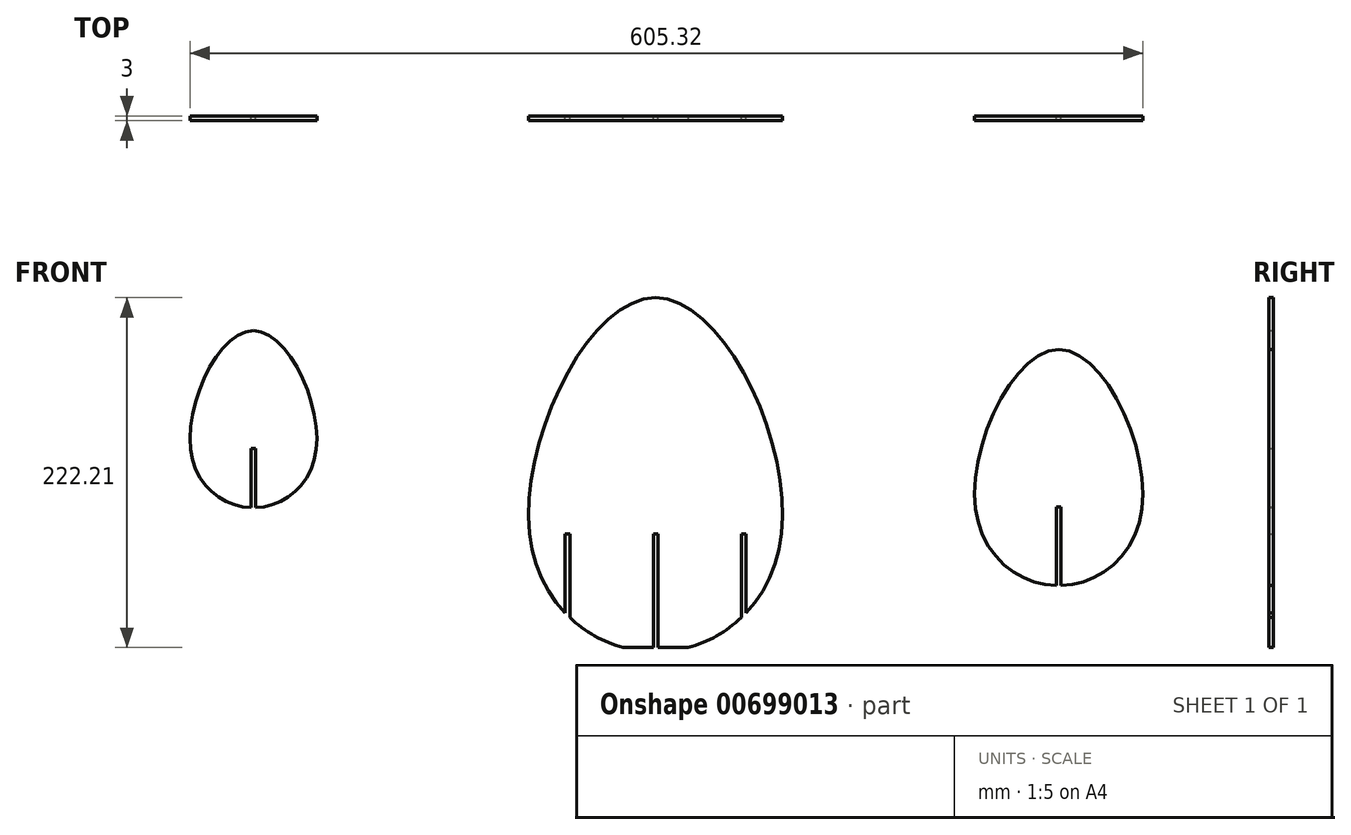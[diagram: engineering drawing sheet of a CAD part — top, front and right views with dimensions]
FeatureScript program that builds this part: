
annotation { "Feature Type Name" : "Feature", "Feature Type Description" : "" }
export const myFeature = defineFeature(function(context is Context, id is Id, definition is map)
    precondition{}
    {
        {
            var Q0;
            Q0=qCreatedBy(makeId("Front.planeOp"),FACE);
            var sketch = newSketch(context, id + "F0", { "sketchPlane" : qUnion([Q0])});
            skLineSegment(sketch, "E0", {"start": v(0, 0) * mm, "end": v(-80, 0) * mm, "construction": true});
            skLineSegment(sketch, "E1", {"start": v(0, 0) * mm, "end": v(0, -75) * mm});
            skLineSegment(sketch, "E2", {"start": v(0, 0) * mm, "end": v(80, 0) * mm, "construction": true});
            skLineSegment(sketch, "E3", {"start": v(0, 0) * mm, "end": v(0, 150) * mm});
            skFitSpline(sketch, "E4", {"points": [v(0, 150) * mm, v(-80, 0) * mm, v(0, -75) * mm, v(80, 0) * mm, v(0, 150) * mm]});
            skLineSegment(sketch, "E5", {"start": v(-20.64, -72.2) * mm, "end": v(20.64, -72.2) * mm});
            skLineSegment(sketch, "E6", {"start": v(-255.53, 54.14) * mm, "end": v(-295.53, 54.14) * mm, "construction": true});
            skLineSegment(sketch, "E7", {"start": v(-255.53, 54.14) * mm, "end": v(-255.53, 16.64) * mm});
            skLineSegment(sketch, "E8", {"start": v(-255.53, 54.14) * mm, "end": v(-215.53, 54.14) * mm, "construction": true});
            skLineSegment(sketch, "E9", {"start": v(-255.53, 54.14) * mm, "end": v(-255.53, 129.14) * mm});
            skFitSpline(sketch, "E10", {"points": [v(-255.53, 129.14) * mm, v(-295.53, 54.14) * mm, v(-255.53, 16.64) * mm, v(-215.53, 54.14) * mm, v(-255.53, 129.14) * mm]});
            skLineSegment(sketch, "E11", {"start": v(256.02, 17.1) * mm, "end": v(203.02, 17.1) * mm, "construction": true});
            skLineSegment(sketch, "E12", {"start": v(256.02, 17.1) * mm, "end": v(256.02, -32.9) * mm});
            skLineSegment(sketch, "E13", {"start": v(256.02, 17.1) * mm, "end": v(309.02, 17.1) * mm, "construction": true});
            skLineSegment(sketch, "E14", {"start": v(256.02, 17.1) * mm, "end": v(256.02, 117.1) * mm});
            skFitSpline(sketch, "E15", {"points": [v(256.02, 117.1) * mm, v(203.02, 17.1) * mm, v(256.02, -32.9) * mm, v(309.02, 17.1) * mm, v(256.02, 117.1) * mm]});
            skLineSegment(sketch, "E16.bottom", {"start": v(254.52, 17.1) * mm, "end": v(257.52, 17.1) * mm});
            skLineSegment(sketch, "E16.top", {"start": v(254.52, -35.3) * mm, "end": v(257.52, -35.3) * mm});
            skLineSegment(sketch, "E16.left", {"start": v(254.52, 17.1) * mm, "end": v(254.52, -35.3) * mm});
            skLineSegment(sketch, "E16.right", {"start": v(257.52, 17.1) * mm, "end": v(257.52, -35.3) * mm});
            skLineSegment(sketch, "E17.bottom", {"start": v(-257.03, 54.14) * mm, "end": v(-254.03, 54.14) * mm});
            skLineSegment(sketch, "E17.top", {"start": v(-257.03, 14.08) * mm, "end": v(-254.03, 14.08) * mm});
            skLineSegment(sketch, "E17.left", {"start": v(-257.03, 54.14) * mm, "end": v(-257.03, 14.08) * mm});
            skLineSegment(sketch, "E17.right", {"start": v(-254.03, 54.14) * mm, "end": v(-254.03, 14.08) * mm});
            skLineSegment(sketch, "E18", {"start": v(54.5, -277) * mm, "end": v(-25.5, -277) * mm, "construction": true});
            skLineSegment(sketch, "E19", {"start": v(54.5, -277) * mm, "end": v(54.5, -352) * mm});
            skLineSegment(sketch, "E20", {"start": v(54.5, -277) * mm, "end": v(134.5, -277) * mm, "construction": true});
            skLineSegment(sketch, "E21", {"start": v(54.5, -277) * mm, "end": v(54.5, -127) * mm});
            skFitSpline(sketch, "E22", {"points": [v(54.5, -127) * mm, v(-25.5, -277) * mm, v(54.5, -352) * mm, v(134.5, -277) * mm, v(54.5, -127) * mm]});
            skLineSegment(sketch, "E23", {"start": v(33.86, -349.21) * mm, "end": v(75.14, -349.21) * mm});
            skLineSegment(sketch, "E24", {"start": v(-211.8, -225.01) * mm, "end": v(-251.8, -225.01) * mm, "construction": true});
            skLineSegment(sketch, "E25", {"start": v(-211.8, -225.01) * mm, "end": v(-211.8, -262.51) * mm});
            skLineSegment(sketch, "E26", {"start": v(-211.8, -225.01) * mm, "end": v(-171.8, -225.01) * mm, "construction": true});
            skLineSegment(sketch, "E27", {"start": v(-211.8, -225.01) * mm, "end": v(-211.8, -150.01) * mm});
            skFitSpline(sketch, "E28", {"points": [v(-211.8, -150.01) * mm, v(-251.8, -225.01) * mm, v(-211.8, -262.51) * mm, v(-171.8, -225.01) * mm, v(-211.8, -150.01) * mm]});
            skLineSegment(sketch, "E29", {"start": v(299.74, -262.05) * mm, "end": v(246.74, -262.05) * mm, "construction": true});
            skLineSegment(sketch, "E30", {"start": v(299.74, -262.05) * mm, "end": v(299.74, -312.05) * mm});
            skLineSegment(sketch, "E31", {"start": v(299.74, -262.05) * mm, "end": v(352.74, -262.05) * mm, "construction": true});
            skLineSegment(sketch, "E32", {"start": v(299.74, -262.05) * mm, "end": v(299.74, -162.05) * mm});
            skFitSpline(sketch, "E33", {"points": [v(299.74, -162.05) * mm, v(246.74, -262.05) * mm, v(299.74, -312.05) * mm, v(352.74, -262.05) * mm, v(299.74, -162.05) * mm]});
            skLineSegment(sketch, "E34.bottom", {"start": v(298.24, -262.05) * mm, "end": v(301.24, -262.05) * mm});
            skLineSegment(sketch, "E35.bottom", {"start": v(-213.3, -225.01) * mm, "end": v(-210.3, -225.01) * mm});
            skLineSegment(sketch, "E36.bottom", {"start": v(-1.5, 0) * mm, "end": v(1.5, 0) * mm});
            skLineSegment(sketch, "E36.top", {"start": v(-1.5, -77.56) * mm, "end": v(1.5, -77.56) * mm});
            skLineSegment(sketch, "E36.left", {"start": v(-1.5, 0) * mm, "end": v(-1.5, -77.56) * mm});
            skLineSegment(sketch, "E36.right", {"start": v(1.5, 0) * mm, "end": v(1.5, -77.56) * mm});
            skLineSegment(sketch, "E37.bottom", {"start": v(56, -277) * mm, "end": v(53, -277) * mm});
            skLineSegment(sketch, "E37.top", {"start": v(56, -127.78) * mm, "end": v(53, -127.78) * mm});
            skLineSegment(sketch, "E37.left", {"start": v(56, -277) * mm, "end": v(56, -127.78) * mm});
            skLineSegment(sketch, "E37.right", {"start": v(53, -277) * mm, "end": v(53, -127.78) * mm});
            skLineSegment(sketch, "E38.bottom", {"start": v(301.24, -262.05) * mm, "end": v(298.24, -262.05) * mm});
            skLineSegment(sketch, "E38.top", {"start": v(301.24, -159.13) * mm, "end": v(298.24, -159.13) * mm});
            skLineSegment(sketch, "E38.left", {"start": v(301.24, -262.05) * mm, "end": v(301.24, -159.13) * mm});
            skLineSegment(sketch, "E38.right", {"start": v(298.24, -262.05) * mm, "end": v(298.24, -159.13) * mm});
            skLineSegment(sketch, "E39.top", {"start": v(-213.3, -147.5) * mm, "end": v(-210.3, -147.5) * mm});
            skLineSegment(sketch, "E39.left", {"start": v(-213.3, -225.01) * mm, "end": v(-213.3, -147.5) * mm});
            skLineSegment(sketch, "E39.right", {"start": v(-210.3, -225.01) * mm, "end": v(-210.3, -147.5) * mm});
            skLineSegment(sketch, "E40.bottom", {"start": v(0, -277) * mm, "end": v(-3, -277) * mm});
            skLineSegment(sketch, "E40.top", {"start": v(0, -167) * mm, "end": v(-3, -167) * mm});
            skLineSegment(sketch, "E40.left", {"start": v(0, -277) * mm, "end": v(0, -167) * mm});
            skLineSegment(sketch, "E40.right", {"start": v(-3, -277) * mm, "end": v(-3, -167) * mm});
            skLineSegment(sketch, "E41.bottom", {"start": v(109, -277) * mm, "end": v(112, -277) * mm});
            skLineSegment(sketch, "E41.top", {"start": v(109, -167) * mm, "end": v(112, -167) * mm});
            skLineSegment(sketch, "E41.left", {"start": v(109, -277) * mm, "end": v(109, -167) * mm});
            skLineSegment(sketch, "E41.right", {"start": v(112, -277) * mm, "end": v(112, -167) * mm});
            skLineSegment(sketch, "E42.bottom", {"start": v(-54.5, 0) * mm, "end": v(-57.5, 0) * mm});
            skLineSegment(sketch, "E42.top", {"start": v(-54.5, -55) * mm, "end": v(-57.5, -55) * mm});
            skLineSegment(sketch, "E42.left", {"start": v(-54.5, 0) * mm, "end": v(-54.5, -55) * mm});
            skLineSegment(sketch, "E42.right", {"start": v(-57.5, 0) * mm, "end": v(-57.5, -55) * mm});
            skLineSegment(sketch, "E43.bottom", {"start": v(54.5, 0) * mm, "end": v(57.5, 0) * mm});
            skLineSegment(sketch, "E43.top", {"start": v(54.5, -55) * mm, "end": v(57.5, -55) * mm});
            skLineSegment(sketch, "E43.left", {"start": v(54.5, 0) * mm, "end": v(54.5, -55) * mm});
            skLineSegment(sketch, "E43.right", {"start": v(57.5, 0) * mm, "end": v(57.5, -55) * mm});
            skSolve(sketch);
        }
        {
            var Q0;
            {var subQ0=sQuery(id+"F0.wireOp",EDGE,"E3");Q0=makeQuery(id+"F0.imprint","IMPRINT",FACE,{"disambiguationData":[TD([[makeQuery(id+"F0.imprint","IMPRINT",EDGE,{"derivedFrom":subQ0}),1.0]])]});}
            var Q1;
            {var subQ0=sQuery(id+"F0.wireOp",EDGE,"E3");Q1=makeQuery(id+"F0.imprint","IMPRINT",FACE,{"disambiguationData":[TD([[makeQuery(id+"F0.imprint","IMPRINT",EDGE,{"derivedFrom":subQ0}),-1.0]])]});}
            var Q2;
            {var subQ0=sQuery(id+"F0.wireOp",EDGE,"E9");Q2=makeQuery(id+"F0.imprint","IMPRINT",FACE,{"disambiguationData":[TD([[makeQuery(id+"F0.imprint","IMPRINT",EDGE,{"derivedFrom":subQ0}),-1.0]])]});}
            var Q3;
            {var subQ0=sQuery(id+"F0.wireOp",EDGE,"E9");Q3=makeQuery(id+"F0.imprint","IMPRINT",FACE,{"disambiguationData":[TD([[makeQuery(id+"F0.imprint","IMPRINT",EDGE,{"derivedFrom":subQ0}),1.0]])]});}
            var Q4;
            {var subQ0=sQuery(id+"F0.wireOp",EDGE,"E14");Q4=makeQuery(id+"F0.imprint","IMPRINT",FACE,{"disambiguationData":[TD([[makeQuery(id+"F0.imprint","IMPRINT",EDGE,{"derivedFrom":subQ0}),1.0]])]});}
            var Q5;
            {var subQ0=sQuery(id+"F0.wireOp",EDGE,"E14");Q5=makeQuery(id+"F0.imprint","IMPRINT",FACE,{"disambiguationData":[TD([[makeQuery(id+"F0.imprint","IMPRINT",EDGE,{"derivedFrom":subQ0}),-1.0]])]});}
            extrude(context, id + "F1", {"entities" : qUnion([Q0, Q1, Q2, Q3, Q4, Q5]), "depth" : 3 * mm, "offsetDistance" : 25 * mm});
        }
    });
